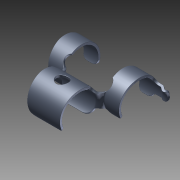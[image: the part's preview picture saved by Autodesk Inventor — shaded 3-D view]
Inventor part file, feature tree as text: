
AUTODESK INVENTOR PART (.ipt)
format: ipt  version: 2013 (Build 170138000, 138)  size: 2,241,536 bytes
history: native  units: mm
features: other x1, plane x1, emboss x1, imported_body x1, sketch x1
ambient origin geometry x8: Origin, YZ Plane, XZ Plane, XY Plane, X Axis, Y Axis, Z Axis, Center Point
feature tree (5):
  other  "M13 clip solid1"
  plane  "Work Plane2"
  emboss  "Emboss1"
  imported_body  "Base1"
  sketch  "Sketch2"  dims[d22=-8.0mm d23=0.5mm d24=0.0mm]
